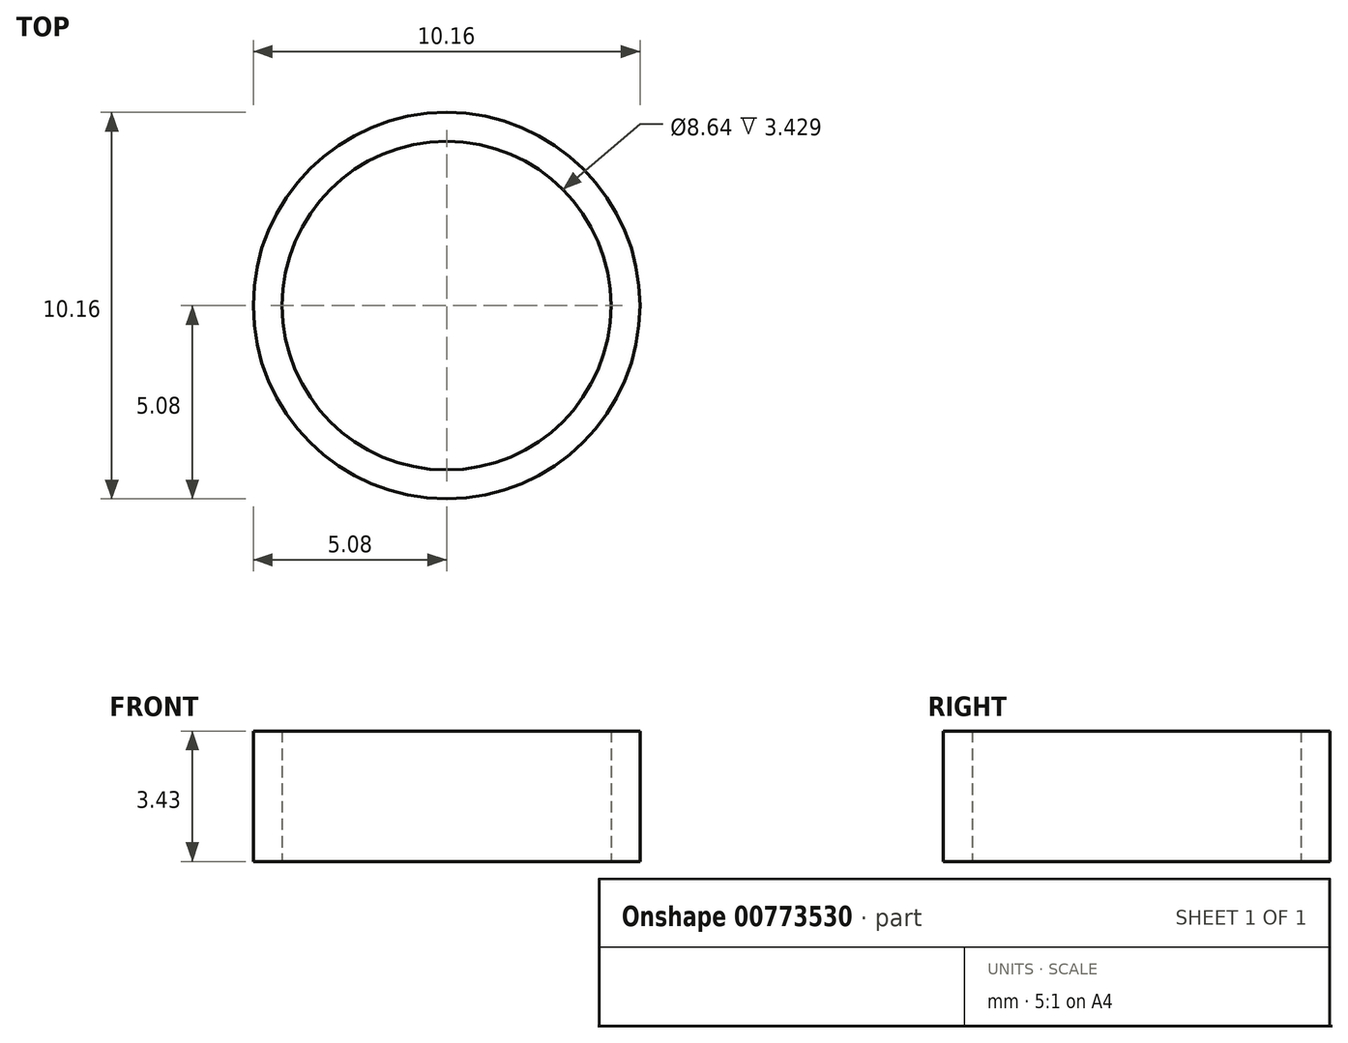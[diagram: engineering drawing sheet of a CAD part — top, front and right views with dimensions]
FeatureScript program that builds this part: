
annotation { "Feature Type Name" : "Feature", "Feature Type Description" : "" }
export const myFeature = defineFeature(function(context is Context, id is Id, definition is map)
    precondition{}
    {
        {
            var Q0;
            Q0=qCreatedBy(makeId("Top.planeOp"),FACE);
            var sketch = newSketch(context, id + "F0", { "sketchPlane" : qUnion([Q0])});
            skCircle(sketch, "E0", {"center": v(0, 0) * mm, "radius": 4.32 * mm});
            skCircle(sketch, "E1.0", {"center": v(0, 0) * mm, "radius": 5.08 * mm});
            skSolve(sketch);
        }
        {
            var Q0;
            Q0=makeQuery(id+"F0.imprint","IMPRINT",FACE,{"disambiguationData":[TD([[makeQuery(id+"F0.imprint","IMPRINT",EDGE,{"derivedFrom":sQuery(id+"F0.wireOp",EDGE,"E0")}),-1.0]])]});
            extrude(context, id + "F1", {"entities" : qUnion([Q0]), "depth" : 3.43 * mm, "offsetDistance" : 25.4 * mm});
        }
    });
